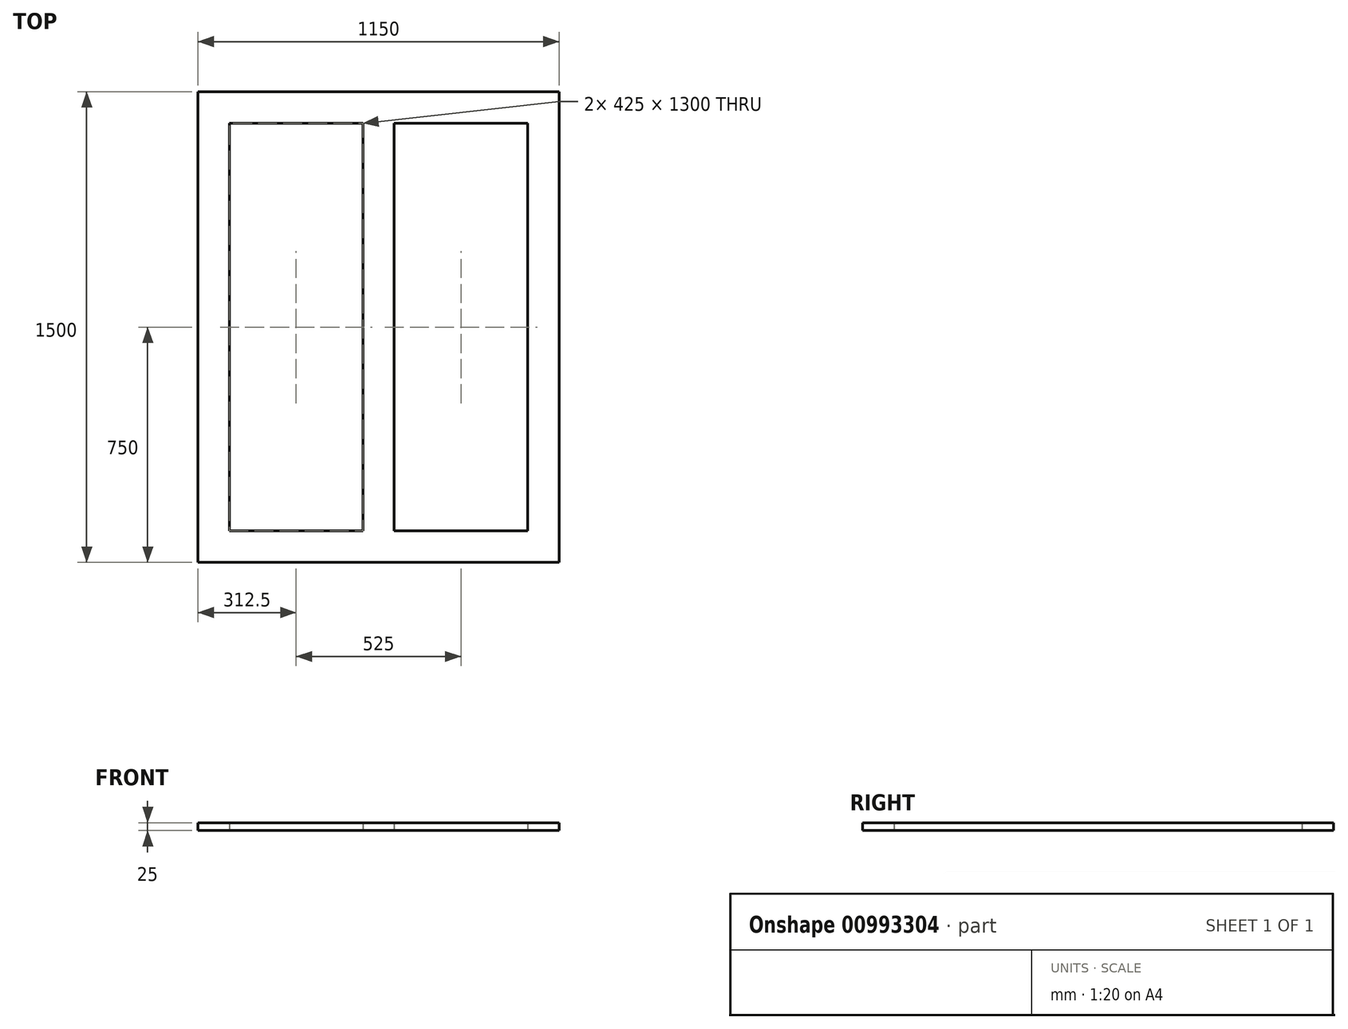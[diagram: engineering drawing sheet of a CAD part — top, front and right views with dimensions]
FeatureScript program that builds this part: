
annotation { "Feature Type Name" : "Feature", "Feature Type Description" : "" }
export const myFeature = defineFeature(function(context is Context, id is Id, definition is map)
    precondition{}
    {
        {
            var Q0;
            Q0=qCreatedBy(makeId("Top.planeOp"),FACE);
            var sketch = newSketch(context, id + "F0", { "sketchPlane" : qUnion([Q0])});
            skLineSegment(sketch, "E0.bottom", {"start": v(0, 1500) * mm, "end": v(1150, 1500) * mm});
            skLineSegment(sketch, "E0.top", {"start": v(0, 0) * mm, "end": v(1150, 0) * mm});
            skLineSegment(sketch, "E0.left", {"start": v(0, 1500) * mm, "end": v(0, 0) * mm});
            skLineSegment(sketch, "E0.right", {"start": v(1150, 1500) * mm, "end": v(1150, 0) * mm});
            skSolve(sketch);
        }
        {
            var Q0;
            Q0=makeQuery(id+"F0.imprint","IMPRINT",FACE,{"disambiguationData":[TD([[makeQuery(id+"F0.imprint","IMPRINT",EDGE,{"derivedFrom":sQuery(id+"F0.wireOp",EDGE,"E0.bottom")}),-1.0]])]});
            extrude(context, id + "F1", {"entities" : qUnion([Q0]), "depth" : 25 * mm, "offsetDistance" : 25 * mm});
        }
        {
            var Q0;
            Q0=qCreatedBy(makeId("Top.planeOp"),FACE);
            var sketch = newSketch(context, id + "F2", { "sketchPlane" : qUnion([Q0])});
            skLineSegment(sketch, "E1.bottom", {"start": v(100, 100) * mm, "end": v(525, 100) * mm});
            skLineSegment(sketch, "E1.top", {"start": v(100, 1400) * mm, "end": v(525, 1400) * mm});
            skLineSegment(sketch, "E1.left", {"start": v(100, 100) * mm, "end": v(100, 1400) * mm});
            skLineSegment(sketch, "E1.right", {"start": v(525, 100) * mm, "end": v(525, 1400) * mm});
            skLineSegment(sketch, "E2.bottom", {"start": v(625, 1400) * mm, "end": v(1050, 1400) * mm});
            skLineSegment(sketch, "E2.top", {"start": v(625, 100) * mm, "end": v(1050, 100) * mm});
            skLineSegment(sketch, "E2.left", {"start": v(625, 1400) * mm, "end": v(625, 100) * mm});
            skLineSegment(sketch, "E2.right", {"start": v(1050, 1400) * mm, "end": v(1050, 100) * mm});
            skSolve(sketch);
        }
        {
            var Q0;
            Q0=makeQuery(id+"F2.imprint","IMPRINT",FACE,{"disambiguationData":[TD([[makeQuery(id+"F2.imprint","IMPRINT",EDGE,{"derivedFrom":sQuery(id+"F2.wireOp",EDGE,"E1.bottom")}),1.0]])]});
            var Q1;
            Q1=makeQuery(id+"F2.imprint","IMPRINT",FACE,{"disambiguationData":[TD([[makeQuery(id+"F2.imprint","IMPRINT",EDGE,{"derivedFrom":sQuery(id+"F2.wireOp",EDGE,"E2.bottom")}),-1.0]])]});
            extrude(context, id + "F3", {"entities" : qUnion([Q0, Q1]), "operationType" : NewBodyOperationType.REMOVE, "depth" : 25 * mm, "offsetDistance" : 25 * mm});
        }
    });
